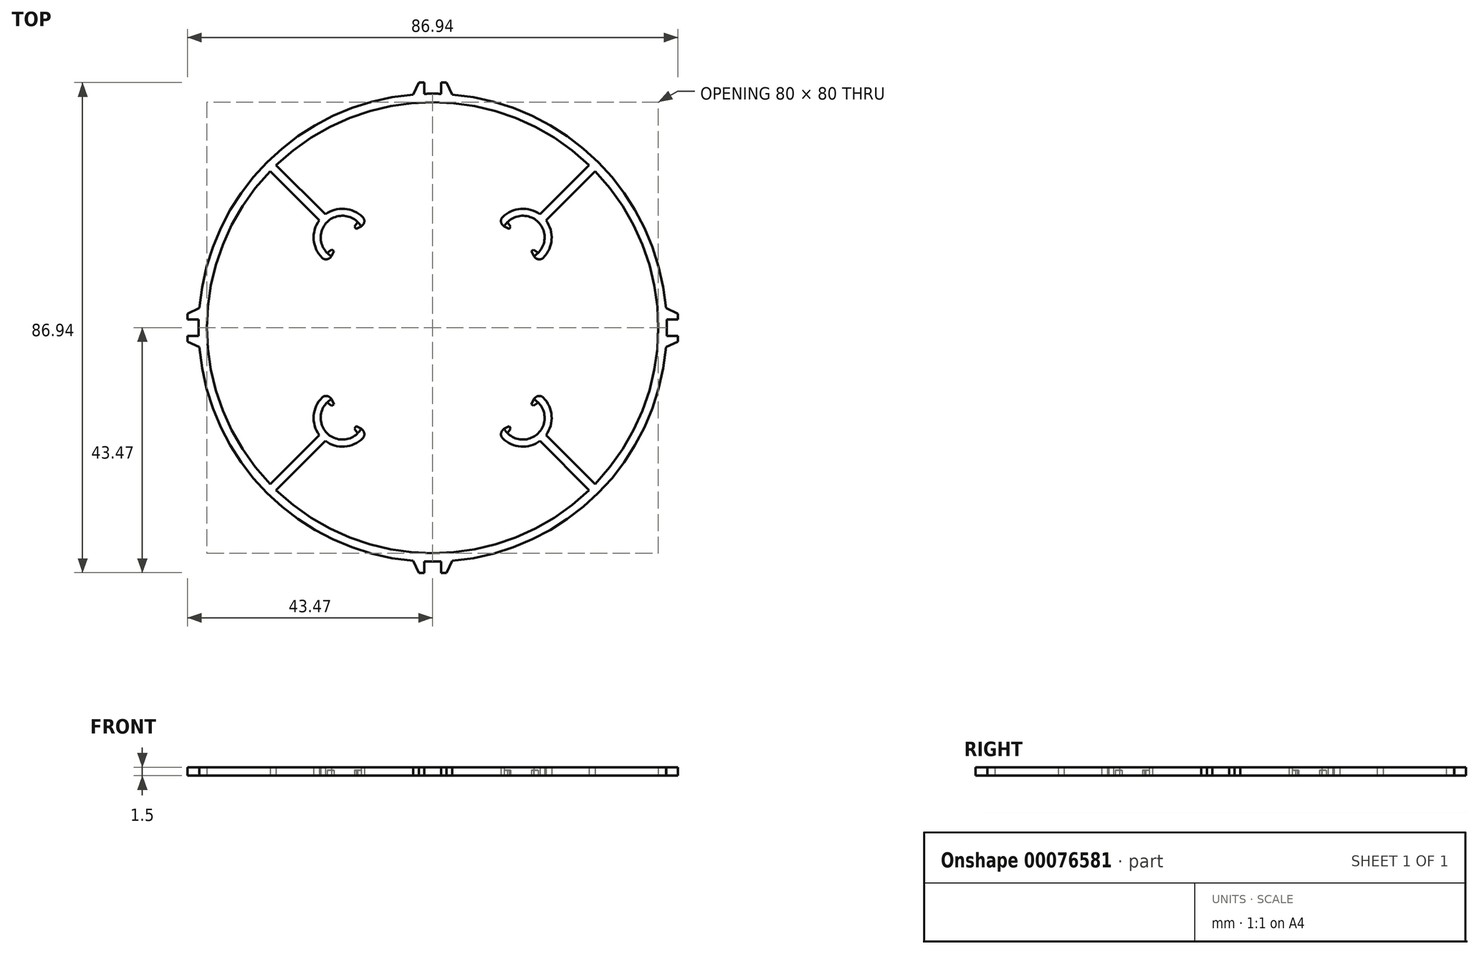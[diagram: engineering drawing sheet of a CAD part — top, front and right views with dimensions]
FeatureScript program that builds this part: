
annotation { "Feature Type Name" : "Feature", "Feature Type Description" : "" }
export const myFeature = defineFeature(function(context is Context, id is Id, definition is map)
    precondition{}
    {
        {
            var Q0;
            Q0=qCreatedBy(makeId("Top.planeOp"),FACE);
            var sketch = newSketch(context, id + "F0", { "sketchPlane" : qUnion([Q0])});
            skLineSegment(sketch, "E0.bottom", {"start": v(-16, 16) * mm, "end": v(16, 16) * mm});
            skLineSegment(sketch, "E0.top", {"start": v(-16, -16) * mm, "end": v(16, -16) * mm});
            skLineSegment(sketch, "E0.left", {"start": v(-16, 16) * mm, "end": v(-16, -16) * mm});
            skLineSegment(sketch, "E0.right", {"start": v(16, 16) * mm, "end": v(16, -16) * mm});
            skPoint(sketch, "E0.middle", {"position": v(0, 0) * mm});
            skCircle(sketch, "E1", {"center": v(-16, 16) * mm, "radius": 15 * mm});
            skCircle(sketch, "E2", {"center": v(16, 16) * mm, "radius": 15 * mm});
            skCircle(sketch, "E3", {"center": v(-16, -16) * mm, "radius": 15 * mm});
            skCircle(sketch, "E4", {"center": v(16, -16) * mm, "radius": 15 * mm});
            skLineSegment(sketch, "E5.bottom", {"start": v(-10, 10) * mm, "end": v(10, 10) * mm});
            skLineSegment(sketch, "E5.top", {"start": v(-10, -10) * mm, "end": v(10, -10) * mm});
            skLineSegment(sketch, "E5.left", {"start": v(-10, 10) * mm, "end": v(-10, -10) * mm});
            skLineSegment(sketch, "E5.right", {"start": v(10, 10) * mm, "end": v(10, -10) * mm});
            skCircle(sketch, "E6", {"center": v(-16, 16) * mm, "radius": 4.5 * mm});
            skCircle(sketch, "E7", {"center": v(-16, 16) * mm, "radius": 3.5 * mm});
            skCircle(sketch, "E8", {"center": v(16, 16) * mm, "radius": 3.5 * mm});
            skCircle(sketch, "E9", {"center": v(16, 16) * mm, "radius": 4.5 * mm});
            skCircle(sketch, "E10", {"center": v(16, -16) * mm, "radius": 4.5 * mm});
            skCircle(sketch, "E11", {"center": v(16, -16) * mm, "radius": 3.5 * mm});
            skCircle(sketch, "E12", {"center": v(-16, -16) * mm, "radius": 3.5 * mm});
            skCircle(sketch, "E13", {"center": v(-16, -16) * mm, "radius": 4.5 * mm});
            skLineSegment(sketch, "E14.bottom", {"start": v(-16, 16) * mm, "end": v(-11, 16) * mm});
            skLineSegment(sketch, "E14.left", {"start": v(-16, 16) * mm, "end": v(-16, 21) * mm});
            skLineSegment(sketch, "E15", {"start": v(-12.82, 19.18) * mm, "end": v(-19.18, 12.82) * mm});
            skLineSegment(sketch, "E16", {"start": v(-18.4, 12.2) * mm, "end": v(-12.2, 18.4) * mm});
            skSolve(sketch);
        }
        {
            var Q0;
            {var subQ1=sQuery(id+"F0.wireOp",EDGE,"E0.bottom");var subQ5=sQuery(id+"F0.wireOp",EDGE,"E14.bottom");var subQ6=makeQuery(id+"F0.imprint","INTERSECT",VERTEX,{"derivedFrom":[subQ1,subQ5]});Q0=makeQuery(id+"F0.imprint","IMPRINT",FACE,{"disambiguationData":[TD([[makeQuery(id+"F0.imprint","IMPRINT",EDGE,{"disambiguationData":[TD([[subQ6,-1.0]])],"derivedFrom":subQ1}),1.0]])]});}
            var sketch = newSketch(context, id + "F1", { "sketchPlane" : qUnion([Q0])});
            skArc(sketch, "E17", {"start": v(-28.8, 27.75) * mm, "mid": v(-40, 0) * mm, "end": v(-28.8, -27.75) * mm});
            skCircle(sketch, "E18", {"center": v(0, 0) * mm, "radius": 41.5 * mm});
            skArc(sketch, "E19", {"start": v(-13.28, 18.72) * mm, "mid": v(-18.72, 18.72) * mm, "end": v(-18.72, 13.28) * mm});
            skArc(sketch, "E20", {"start": v(-12.4, 19.62) * mm, "mid": v(-15.63, 21.09) * mm, "end": v(-19.04, 20.1) * mm});
            skLineSegment(sketch, "E21", {"start": v(-17.93, 12.67) * mm, "end": v(-17.49, 13.57) * mm});
            skLineSegment(sketch, "E22", {"start": v(-17.49, 13.57) * mm, "end": v(-17.9, 13.85) * mm});
            skLineSegment(sketch, "E23", {"start": v(-17.9, 13.85) * mm, "end": v(-18.72, 13.28) * mm});
            skLineSegment(sketch, "E24", {"start": v(-13.28, 18.72) * mm, "end": v(-13.85, 17.9) * mm});
            skLineSegment(sketch, "E25", {"start": v(-13.85, 17.9) * mm, "end": v(-13.57, 17.49) * mm});
            skLineSegment(sketch, "E26", {"start": v(-13.57, 17.49) * mm, "end": v(-12.67, 17.93) * mm});
            skLineSegment(sketch, "E27", {"start": v(-19.04, 20.1) * mm, "end": v(-27.75, 28.8) * mm});
            skLineSegment(sketch, "E28", {"start": v(-20.1, 19.04) * mm, "end": v(-28.8, 27.75) * mm});
            skLineSegment(sketch, "E29", {"start": v(-18.2, 12.4) * mm, "end": v(-17.93, 12.67) * mm});
            skLineSegment(sketch, "E30", {"start": v(-12.4, 18.2) * mm, "end": v(-12.67, 17.93) * mm});
            skPoint(sketch, "E31.visualSharp", {"position": v(-18.84, 11.76) * mm});
            skArc(sketch, "E31.filletArc", {"start": v(-19.62, 12.4) * mm, "mid": v(-18.9, 12.1) * mm, "end": v(-18.2, 12.4) * mm});
            skPoint(sketch, "E32.visualSharp", {"position": v(-11.76, 18.84) * mm});
            skArc(sketch, "E32.filletArc", {"start": v(-12.4, 18.2) * mm, "mid": v(-12.1, 18.9) * mm, "end": v(-12.4, 19.62) * mm});
            skArc(sketch, "E33.trimOffspring", {"start": v(-20.1, 19.04) * mm, "mid": v(-21.09, 15.63) * mm, "end": v(-19.62, 12.4) * mm});
            skArc(sketch, "E34.1.0", {"start": v(-19.62, -12.4) * mm, "mid": v(-21.09, -15.63) * mm, "end": v(-20.1, -19.04) * mm});
            skPoint(sketch, "E34.1.1", {"position": v(-18.84, -11.76) * mm});
            skLineSegment(sketch, "E34.1.2", {"start": v(-20.1, -19.04) * mm, "end": v(-28.8, -27.75) * mm});
            skLineSegment(sketch, "E34.1.3", {"start": v(-19.04, -20.1) * mm, "end": v(-27.75, -28.8) * mm});
            skPoint(sketch, "E34.1.4", {"position": v(-11.76, -18.84) * mm});
            skArc(sketch, "E34.1.5", {"start": v(-19.04, -20.1) * mm, "mid": v(-15.63, -21.09) * mm, "end": v(-12.4, -19.62) * mm});
            skArc(sketch, "E34.1.6", {"start": v(-18.72, -13.28) * mm, "mid": v(-18.72, -18.72) * mm, "end": v(-13.28, -18.72) * mm});
            skArc(sketch, "E34.1.7", {"start": v(-18.2, -12.4) * mm, "mid": v(-18.9, -12.1) * mm, "end": v(-19.62, -12.4) * mm});
            skLineSegment(sketch, "E34.1.8", {"start": v(-13.57, -17.49) * mm, "end": v(-13.85, -17.9) * mm});
            skLineSegment(sketch, "E34.1.9", {"start": v(-13.85, -17.9) * mm, "end": v(-13.28, -18.72) * mm});
            skLineSegment(sketch, "E34.1.10", {"start": v(-18.72, -13.28) * mm, "end": v(-17.9, -13.85) * mm});
            skLineSegment(sketch, "E34.1.11", {"start": v(-17.9, -13.85) * mm, "end": v(-17.49, -13.57) * mm});
            skLineSegment(sketch, "E34.1.12", {"start": v(-17.49, -13.57) * mm, "end": v(-17.93, -12.67) * mm});
            skLineSegment(sketch, "E34.1.13", {"start": v(-18.2, -12.4) * mm, "end": v(-17.93, -12.67) * mm});
            skLineSegment(sketch, "E34.1.14", {"start": v(-18.2, -12.4) * mm, "end": v(-17.93, -12.67) * mm});
            skLineSegment(sketch, "E34.1.15", {"start": v(-12.67, -17.93) * mm, "end": v(-13.57, -17.49) * mm});
            skArc(sketch, "E34.1.16", {"start": v(-12.4, -19.62) * mm, "mid": v(-12.1, -18.9) * mm, "end": v(-12.4, -18.2) * mm});
            skLineSegment(sketch, "E34.1.17", {"start": v(-12.4, -18.2) * mm, "end": v(-12.67, -17.93) * mm});
            skLineSegment(sketch, "E34.1.18", {"start": v(-12.4, -18.2) * mm, "end": v(-12.67, -17.93) * mm});
            skArc(sketch, "E34.2.0", {"start": v(12.4, -19.62) * mm, "mid": v(15.63, -21.09) * mm, "end": v(19.04, -20.1) * mm});
            skPoint(sketch, "E34.2.1", {"position": v(11.76, -18.84) * mm});
            skLineSegment(sketch, "E34.2.2", {"start": v(19.04, -20.1) * mm, "end": v(27.75, -28.8) * mm});
            skLineSegment(sketch, "E34.2.3", {"start": v(20.1, -19.04) * mm, "end": v(28.8, -27.75) * mm});
            skPoint(sketch, "E34.2.4", {"position": v(18.84, -11.76) * mm});
            skArc(sketch, "E34.2.5", {"start": v(20.1, -19.04) * mm, "mid": v(21.09, -15.63) * mm, "end": v(19.62, -12.4) * mm});
            skArc(sketch, "E34.2.6", {"start": v(13.28, -18.72) * mm, "mid": v(18.72, -18.72) * mm, "end": v(18.72, -13.28) * mm});
            skArc(sketch, "E34.2.7", {"start": v(12.4, -18.2) * mm, "mid": v(12.1, -18.9) * mm, "end": v(12.4, -19.62) * mm});
            skLineSegment(sketch, "E34.2.8", {"start": v(17.49, -13.57) * mm, "end": v(17.9, -13.85) * mm});
            skLineSegment(sketch, "E34.2.9", {"start": v(17.9, -13.85) * mm, "end": v(18.72, -13.28) * mm});
            skLineSegment(sketch, "E34.2.10", {"start": v(13.28, -18.72) * mm, "end": v(13.85, -17.9) * mm});
            skLineSegment(sketch, "E34.2.11", {"start": v(13.85, -17.9) * mm, "end": v(13.57, -17.49) * mm});
            skLineSegment(sketch, "E34.2.12", {"start": v(13.57, -17.49) * mm, "end": v(12.67, -17.93) * mm});
            skLineSegment(sketch, "E34.2.13", {"start": v(12.4, -18.2) * mm, "end": v(12.67, -17.93) * mm});
            skLineSegment(sketch, "E34.2.14", {"start": v(12.4, -18.2) * mm, "end": v(12.67, -17.93) * mm});
            skLineSegment(sketch, "E34.2.15", {"start": v(17.93, -12.67) * mm, "end": v(17.49, -13.57) * mm});
            skArc(sketch, "E34.2.16", {"start": v(19.62, -12.4) * mm, "mid": v(18.9, -12.1) * mm, "end": v(18.2, -12.4) * mm});
            skLineSegment(sketch, "E34.2.17", {"start": v(18.2, -12.4) * mm, "end": v(17.93, -12.67) * mm});
            skLineSegment(sketch, "E34.2.18", {"start": v(18.2, -12.4) * mm, "end": v(17.93, -12.67) * mm});
            skArc(sketch, "E34.3.0", {"start": v(19.62, 12.4) * mm, "mid": v(21.09, 15.63) * mm, "end": v(20.1, 19.04) * mm});
            skPoint(sketch, "E34.3.1", {"position": v(18.84, 11.76) * mm});
            skLineSegment(sketch, "E34.3.2", {"start": v(20.1, 19.04) * mm, "end": v(28.8, 27.75) * mm});
            skLineSegment(sketch, "E34.3.3", {"start": v(19.04, 20.1) * mm, "end": v(27.75, 28.8) * mm});
            skPoint(sketch, "E34.3.4", {"position": v(11.76, 18.84) * mm});
            skArc(sketch, "E34.3.5", {"start": v(19.04, 20.1) * mm, "mid": v(15.63, 21.09) * mm, "end": v(12.4, 19.62) * mm});
            skArc(sketch, "E34.3.6", {"start": v(18.72, 13.28) * mm, "mid": v(18.72, 18.72) * mm, "end": v(13.28, 18.72) * mm});
            skArc(sketch, "E34.3.7", {"start": v(18.2, 12.4) * mm, "mid": v(18.9, 12.1) * mm, "end": v(19.62, 12.4) * mm});
            skLineSegment(sketch, "E34.3.8", {"start": v(13.57, 17.49) * mm, "end": v(13.85, 17.9) * mm});
            skLineSegment(sketch, "E34.3.9", {"start": v(13.85, 17.9) * mm, "end": v(13.28, 18.72) * mm});
            skLineSegment(sketch, "E34.3.10", {"start": v(18.72, 13.28) * mm, "end": v(17.9, 13.85) * mm});
            skLineSegment(sketch, "E34.3.11", {"start": v(17.9, 13.85) * mm, "end": v(17.49, 13.57) * mm});
            skLineSegment(sketch, "E34.3.12", {"start": v(17.49, 13.57) * mm, "end": v(17.93, 12.67) * mm});
            skLineSegment(sketch, "E34.3.13", {"start": v(18.2, 12.4) * mm, "end": v(17.93, 12.67) * mm});
            skLineSegment(sketch, "E34.3.14", {"start": v(18.2, 12.4) * mm, "end": v(17.93, 12.67) * mm});
            skLineSegment(sketch, "E34.3.15", {"start": v(12.67, 17.93) * mm, "end": v(13.57, 17.49) * mm});
            skArc(sketch, "E34.3.16", {"start": v(12.4, 19.62) * mm, "mid": v(12.1, 18.9) * mm, "end": v(12.4, 18.2) * mm});
            skLineSegment(sketch, "E34.3.17", {"start": v(12.4, 18.2) * mm, "end": v(12.67, 17.93) * mm});
            skLineSegment(sketch, "E34.3.18", {"start": v(12.4, 18.2) * mm, "end": v(12.67, 17.93) * mm});
            skArc(sketch, "E35.trimOffspring", {"start": v(27.75, 28.8) * mm, "mid": v(0, 40) * mm, "end": v(-27.75, 28.8) * mm});
            skArc(sketch, "E36.trimOffspring", {"start": v(-27.75, -28.8) * mm, "mid": v(0, -40) * mm, "end": v(27.75, -28.8) * mm});
            skArc(sketch, "E37.trimOffspring", {"start": v(28.8, -27.75) * mm, "mid": v(40, 0) * mm, "end": v(28.8, 27.75) * mm});
            skSolve(sketch);
        }
        {
            var Q0;
            Q0 = qSketchRegion(id + "F1", true);
            extrude(context, id + "F2", {"entities" : qUnion([Q0]), "depth" : 1.5 * mm});
        }
        {
            var Q0;
            Q0=makeQuery(id+"F2.opExtrude","CAP_FACE",FACE,{"disambiguationData":[OSD([sQuery(id+"F1.wireOp",EDGE,"E17"),sQuery(id+"F1.wireOp",EDGE,"E18"),sQuery(id+"F1.wireOp",EDGE,"E19"),sQuery(id+"F1.wireOp",EDGE,"E20"),sQuery(id+"F1.wireOp",EDGE,"E21"),sQuery(id+"F1.wireOp",EDGE,"E22"),sQuery(id+"F1.wireOp",EDGE,"E23"),sQuery(id+"F1.wireOp",EDGE,"E24"),sQuery(id+"F1.wireOp",EDGE,"E25"),sQuery(id+"F1.wireOp",EDGE,"E26"),sQuery(id+"F1.wireOp",EDGE,"E27"),sQuery(id+"F1.wireOp",EDGE,"E28"),sQuery(id+"F1.wireOp",EDGE,"E31.filletArc"),sQuery(id+"F1.wireOp",EDGE,"E32.filletArc"),sQuery(id+"F1.wireOp",EDGE,"E29"),sQuery(id+"F1.wireOp",EDGE,"E30"),sQuery(id+"F1.wireOp",EDGE,"E33.trimOffspring"),sQuery(id+"F1.wireOp",EDGE,"E34.1.0"),sQuery(id+"F1.wireOp",EDGE,"E34.1.2"),sQuery(id+"F1.wireOp",EDGE,"E34.1.3"),sQuery(id+"F1.wireOp",EDGE,"E34.1.5"),sQuery(id+"F1.wireOp",EDGE,"E34.1.6"),sQuery(id+"F1.wireOp",EDGE,"E34.1.7"),sQuery(id+"F1.wireOp",EDGE,"E34.1.8"),sQuery(id+"F1.wireOp",EDGE,"E34.1.9"),sQuery(id+"F1.wireOp",EDGE,"E34.1.10"),sQuery(id+"F1.wireOp",EDGE,"E34.1.11"),sQuery(id+"F1.wireOp",EDGE,"E34.1.12"),sQuery(id+"F1.wireOp",EDGE,"E34.1.14"),sQuery(id+"F1.wireOp",EDGE,"E34.1.15"),sQuery(id+"F1.wireOp",EDGE,"E34.1.16"),sQuery(id+"F1.wireOp",EDGE,"E34.1.18"),sQuery(id+"F1.wireOp",EDGE,"E34.2.0"),sQuery(id+"F1.wireOp",EDGE,"E34.2.2"),sQuery(id+"F1.wireOp",EDGE,"E34.2.3"),sQuery(id+"F1.wireOp",EDGE,"E34.2.5"),sQuery(id+"F1.wireOp",EDGE,"E34.2.6"),sQuery(id+"F1.wireOp",EDGE,"E34.2.7"),sQuery(id+"F1.wireOp",EDGE,"E34.2.8"),sQuery(id+"F1.wireOp",EDGE,"E34.2.9"),sQuery(id+"F1.wireOp",EDGE,"E34.2.10"),sQuery(id+"F1.wireOp",EDGE,"E34.2.11"),sQuery(id+"F1.wireOp",EDGE,"E34.2.12"),sQuery(id+"F1.wireOp",EDGE,"E34.2.14"),sQuery(id+"F1.wireOp",EDGE,"E34.2.15"),sQuery(id+"F1.wireOp",EDGE,"E34.2.16"),sQuery(id+"F1.wireOp",EDGE,"E34.2.18"),sQuery(id+"F1.wireOp",EDGE,"E34.3.0"),sQuery(id+"F1.wireOp",EDGE,"E34.3.2"),sQuery(id+"F1.wireOp",EDGE,"E34.3.3"),sQuery(id+"F1.wireOp",EDGE,"E34.3.5"),sQuery(id+"F1.wireOp",EDGE,"E34.3.6"),sQuery(id+"F1.wireOp",EDGE,"E34.3.7"),sQuery(id+"F1.wireOp",EDGE,"E34.3.8"),sQuery(id+"F1.wireOp",EDGE,"E34.3.9"),sQuery(id+"F1.wireOp",EDGE,"E34.3.10"),sQuery(id+"F1.wireOp",EDGE,"E34.3.11"),sQuery(id+"F1.wireOp",EDGE,"E34.3.12"),sQuery(id+"F1.wireOp",EDGE,"E34.3.14"),sQuery(id+"F1.wireOp",EDGE,"E34.3.15"),sQuery(id+"F1.wireOp",EDGE,"E34.3.16"),sQuery(id+"F1.wireOp",EDGE,"E34.3.18"),sQuery(id+"F1.wireOp",EDGE,"E35.trimOffspring"),sQuery(id+"F1.wireOp",EDGE,"E36.trimOffspring"),sQuery(id+"F1.wireOp",EDGE,"E37.trimOffspring")])],"isStart":false});
            var sketch = newSketch(context, id + "F3", { "sketchPlane" : qUnion([Q0])});
            skPoint(sketch, "E38.0", {"position": v(-16, 16) * mm});
            skCircle(sketch, "E39", {"center": v(-16, 16) * mm, "radius": 3.85 * mm});
            skCircle(sketch, "E40.1.0", {"center": v(-16, -16) * mm, "radius": 3.85 * mm});
            skCircle(sketch, "E40.2.0", {"center": v(16, -16) * mm, "radius": 3.85 * mm});
            skCircle(sketch, "E40.3.0", {"center": v(16, 16) * mm, "radius": 3.85 * mm});
            skPoint(sketch, "E40.center", {"position": v(0, 0) * mm});
            skSolve(sketch);
        }
        {
            var Q0;
            Q0 = qSketchRegion(id + "F3", true);
            extrude(context, id + "F4", {"entities" : qUnion([Q0]), "operationType" : NewBodyOperationType.REMOVE, "oppositeDirection" : true, "depth" : 0.5 * mm});
        }
        {
            var Q0;
            Q0=qCreatedBy(makeId("Top.planeOp"),FACE);
            var sketch = newSketch(context, id + "F5", { "sketchPlane" : qUnion([Q0])});
            skCircle(sketch, "E41.0", {"center": v(0, 0) * mm, "radius": 41.5 * mm, "construction": true});
            skArc(sketch, "E42.0", {"start": v(27.75, 28.8) * mm, "mid": v(0, 40) * mm, "end": v(-27.75, 28.8) * mm, "construction": true});
            skLineSegment(sketch, "E43", {"start": v(-1.47, 43.47) * mm, "end": v(-2.47, 43.47) * mm});
            skLineSegment(sketch, "E44", {"start": v(-2.47, 43.47) * mm, "end": v(-3.46, 41.36) * mm});
            skLineSegment(sketch, "E45.MirrorCS", {"start": v(1.47, 43.47) * mm, "end": v(2.47, 43.47) * mm});
            skLineSegment(sketch, "E46.MirrorCS", {"start": v(2.47, 43.47) * mm, "end": v(3.46, 41.36) * mm});
            skLineSegment(sketch, "E47", {"start": v(-1.47, 43.47) * mm, "end": v(-1.47, 41.47) * mm});
            skLineSegment(sketch, "E48", {"start": v(1.47, 43.47) * mm, "end": v(1.47, 41.47) * mm});
            skLineSegment(sketch, "E49.1.0", {"start": v(-43.47, 1.47) * mm, "end": v(-43.47, 2.47) * mm});
            skLineSegment(sketch, "E49.1.1", {"start": v(-43.47, -1.47) * mm, "end": v(-43.47, -2.47) * mm});
            skLineSegment(sketch, "E49.1.2", {"start": v(-43.47, 2.47) * mm, "end": v(-41.36, 3.46) * mm});
            skLineSegment(sketch, "E49.1.3", {"start": v(-43.47, -2.47) * mm, "end": v(-41.36, -3.46) * mm});
            skLineSegment(sketch, "E49.1.4", {"start": v(-43.47, 1.47) * mm, "end": v(-41.47, 1.47) * mm});
            skLineSegment(sketch, "E49.1.5", {"start": v(-43.47, -1.47) * mm, "end": v(-41.47, -1.47) * mm});
            skLineSegment(sketch, "E49.2.0", {"start": v(-1.47, -43.47) * mm, "end": v(-2.47, -43.47) * mm});
            skLineSegment(sketch, "E49.2.1", {"start": v(1.47, -43.47) * mm, "end": v(2.47, -43.47) * mm});
            skLineSegment(sketch, "E49.2.2", {"start": v(-2.47, -43.47) * mm, "end": v(-3.46, -41.36) * mm});
            skLineSegment(sketch, "E49.2.3", {"start": v(2.47, -43.47) * mm, "end": v(3.46, -41.36) * mm});
            skLineSegment(sketch, "E49.2.4", {"start": v(-1.47, -43.47) * mm, "end": v(-1.47, -41.47) * mm});
            skLineSegment(sketch, "E49.2.5", {"start": v(1.47, -43.47) * mm, "end": v(1.47, -41.47) * mm});
            skLineSegment(sketch, "E49.3.0", {"start": v(43.47, -1.47) * mm, "end": v(43.47, -2.47) * mm});
            skLineSegment(sketch, "E49.3.1", {"start": v(43.47, 1.47) * mm, "end": v(43.47, 2.47) * mm});
            skLineSegment(sketch, "E49.3.2", {"start": v(43.47, -2.47) * mm, "end": v(41.36, -3.46) * mm});
            skLineSegment(sketch, "E49.3.3", {"start": v(43.47, 2.47) * mm, "end": v(41.36, 3.46) * mm});
            skLineSegment(sketch, "E49.3.4", {"start": v(43.47, -1.47) * mm, "end": v(41.47, -1.47) * mm});
            skLineSegment(sketch, "E49.3.5", {"start": v(43.47, 1.47) * mm, "end": v(41.47, 1.47) * mm});
            skLineSegment(sketch, "E50", {"start": v(-41.47, 1.47) * mm, "end": v(-41.36, 3.46) * mm});
            skLineSegment(sketch, "E51", {"start": v(-41.36, -3.46) * mm, "end": v(-41.47, -1.47) * mm});
            skLineSegment(sketch, "E52", {"start": v(-3.46, 41.36) * mm, "end": v(-1.47, 41.47) * mm});
            skLineSegment(sketch, "E53", {"start": v(1.47, 41.47) * mm, "end": v(3.46, 41.36) * mm});
            skLineSegment(sketch, "E54", {"start": v(41.36, 3.46) * mm, "end": v(41.47, 1.47) * mm});
            skLineSegment(sketch, "E55", {"start": v(41.47, -1.47) * mm, "end": v(41.36, -3.46) * mm});
            skLineSegment(sketch, "E56", {"start": v(1.47, -41.47) * mm, "end": v(3.46, -41.36) * mm});
            skLineSegment(sketch, "E57", {"start": v(-1.47, -41.47) * mm, "end": v(-3.46, -41.36) * mm});
            skSolve(sketch);
        }
        {
            var Q0;
            Q0 = qSketchRegion(id + "F5", true);
            extrude(context, id + "F6", {"entities" : qUnion([Q0]), "operationType" : NewBodyOperationType.ADD, "depth" : 1.5 * mm});
        }
    });
